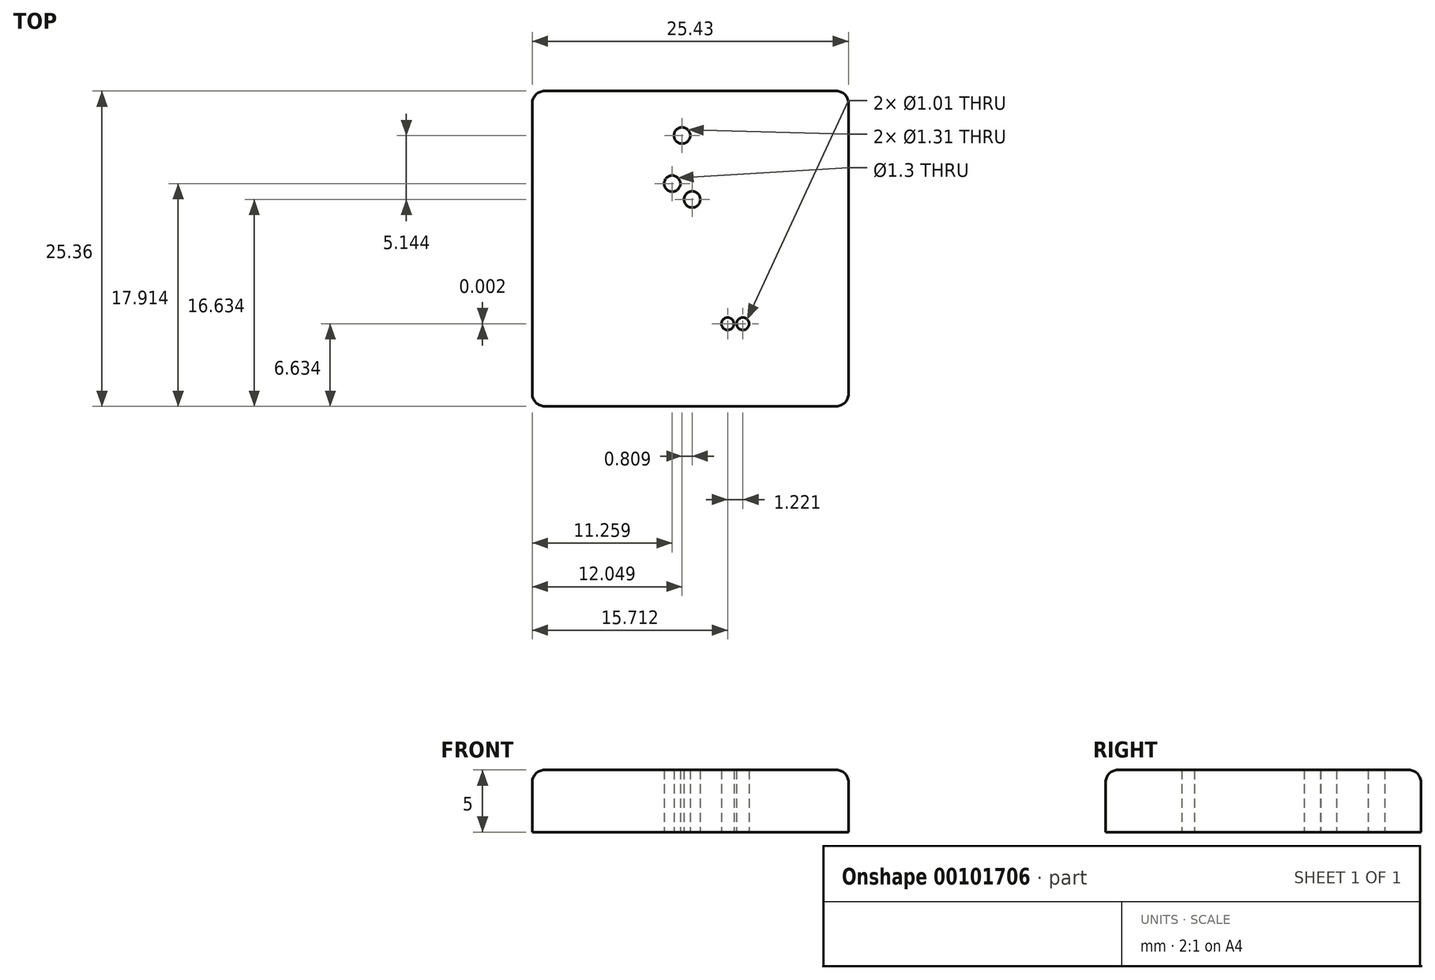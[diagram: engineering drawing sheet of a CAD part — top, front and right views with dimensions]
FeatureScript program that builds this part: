
annotation { "Feature Type Name" : "Feature", "Feature Type Description" : "" }
export const myFeature = defineFeature(function(context is Context, id is Id, definition is map)
    precondition{}
    {
        {
            var Q0;
            Q0=qCreatedBy(makeId("Top.planeOp"),FACE);
            var sketch = newSketch(context, id + "F0", { "sketchPlane" : qUnion([Q0])});
            skCircle(sketch, "E0", {"center": v(-10.56, -18.73) * mm, "radius": 0.5 * mm});
            skCircle(sketch, "E1", {"center": v(-9.34, -18.72) * mm, "radius": 0.5 * mm});
            skCircle(sketch, "E2", {"center": v(-15.01, -7.45) * mm, "radius": 0.65 * mm});
            skCircle(sketch, "E3", {"center": v(-13.41, -8.73) * mm, "radius": 0.65 * mm});
            skCircle(sketch, "E4", {"center": v(-14.22, -3.58) * mm, "radius": 0.65 * mm});
            skLineSegment(sketch, "E5.bottom", {"start": v(-26.27, 0) * mm, "end": v(-0.84, 0) * mm});
            skLineSegment(sketch, "E5.top", {"start": v(-26.27, -25.36) * mm, "end": v(-0.84, -25.36) * mm});
            skLineSegment(sketch, "E5.left", {"start": v(-26.27, 0) * mm, "end": v(-26.27, -25.36) * mm});
            skLineSegment(sketch, "E5.right", {"start": v(-0.84, 0) * mm, "end": v(-0.84, -25.36) * mm});
            skSolve(sketch);
        }
        {
            var Q0;
            Q0=makeQuery(id+"F0.imprint","IMPRINT",FACE,{"disambiguationData":[TD([[makeQuery(id+"F0.imprint","IMPRINT",EDGE,{"derivedFrom":sQuery(id+"F0.wireOp",EDGE,"E0")}),-1.0]])]});
            extrude(context, id + "F1", {"entities" : qUnion([Q0]), "depth" : 5 * mm});
        }
        {
            var Q0;
            Q0=makeQuery(id+"F1.opExtrude","CAP_EDGE",EDGE,{"disambiguationData":[OSD([sQuery(id+"F0.wireOp",EDGE,"E5.bottom")])],"isStart":false});
            fillet(context, id + "F2", {"entities" : qUnion([Q0]), "radius" : 1 * mm, "tangentPropagation" : true, "allowEdgeOverflow" : false});
        }
        {
            var Q0;
            Q0=makeQuery(id+"F1.opExtrude","CAP_EDGE",EDGE,{"disambiguationData":[OSD([sQuery(id+"F0.wireOp",EDGE,"E5.left")])],"isStart":false});
            fillet(context, id + "F3", {"entities" : qUnion([Q0]), "radius" : 1 * mm, "tangentPropagation" : true, "allowEdgeOverflow" : false});
        }
        {
            var Q0;
            Q0=makeQuery(id+"F1.opExtrude","CAP_EDGE",EDGE,{"disambiguationData":[OSD([sQuery(id+"F0.wireOp",EDGE,"E5.top")])],"isStart":false});
            fillet(context, id + "F4", {"entities" : qUnion([Q0]), "radius" : 1 * mm, "tangentPropagation" : true, "allowEdgeOverflow" : false});
        }
        {
            var Q0;
            Q0=makeQuery(id+"F1.opExtrude","CAP_EDGE",EDGE,{"disambiguationData":[OSD([sQuery(id+"F0.wireOp",EDGE,"E5.right")])],"isStart":false});
            fillet(context, id + "F5", {"entities" : qUnion([Q0]), "radius" : 1 * mm, "tangentPropagation" : true, "allowEdgeOverflow" : false});
        }
    });
